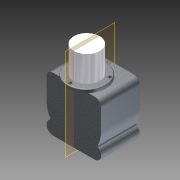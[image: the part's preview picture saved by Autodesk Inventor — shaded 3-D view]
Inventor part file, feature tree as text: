
AUTODESK INVENTOR PART (.ipt)
format: ipt  version: 2014 (Build 180170000, 170)  size: 174,080 bytes
history: native  units: in
note: dims shown in document units (in); Inventor stores cm internally (conversion verified against a paired STEP export)
features: sketch x5, extrude x4, fillet x3, reference x3, projected_geometry x2, hole x1
ambient origin geometry x8: Origin, YZ Plane, XZ Plane, XY Plane, X Axis, Y Axis, Z Axis, Center Point
bodies: Solid1 (feature_tree)
feature tree (18):
  extrude  "Extrusion1"  Depth=2.11in
  fillet  "Fillet1"  Radius=1.5in
  extrude  "Extrusion2"  Depth=0.5in
  fillet  "Fillet2"  Radius=0.5in
  extrude  "Extrusion3"  Depth=1.055in
  fillet  "Fillet3"  Radius=1.0in
  extrude  "Extrusion4"  Depth=1.5in
  hole  "Hole1"  [1 undecoded]
  sketch  "Sketch1"  dims[d0=2.11in d1=2.11in d2=1.5in d3=0.0in]
  sketch  "Sketch3"  dims[d4=0.25in d8=2.0in d9=0.5in]
  sketch  "Sketch4"  dims[d10=0.5in d12=1.055in d13=1.0in d14=0.0in]
  projected_geometry  "Projected Loop1"
  projected_geometry  "Projected Loop2"
  sketch  "Sketch5"  dims[d15=0.0625in d16=1.5in]
  sketch  "Sketch6"  dims[d17=0.25in d18=0.125in d19=0.0in d20=0.0312in d22=1.0in d23=0.0in d24=0.25in d25=0.129in d26=0.75in d27=0.225in d28=0.25in d29=0.5635in d30=0.25in d31=0.8108in]
  reference  "Reference1"
  reference  "Reference2"
  reference  "Reference3"
note: 1 required parameter value undecoded (feature->parameter linkage not recoverable at this tier; creation-order binding heuristic only, values carry confidence <= 0.55)
